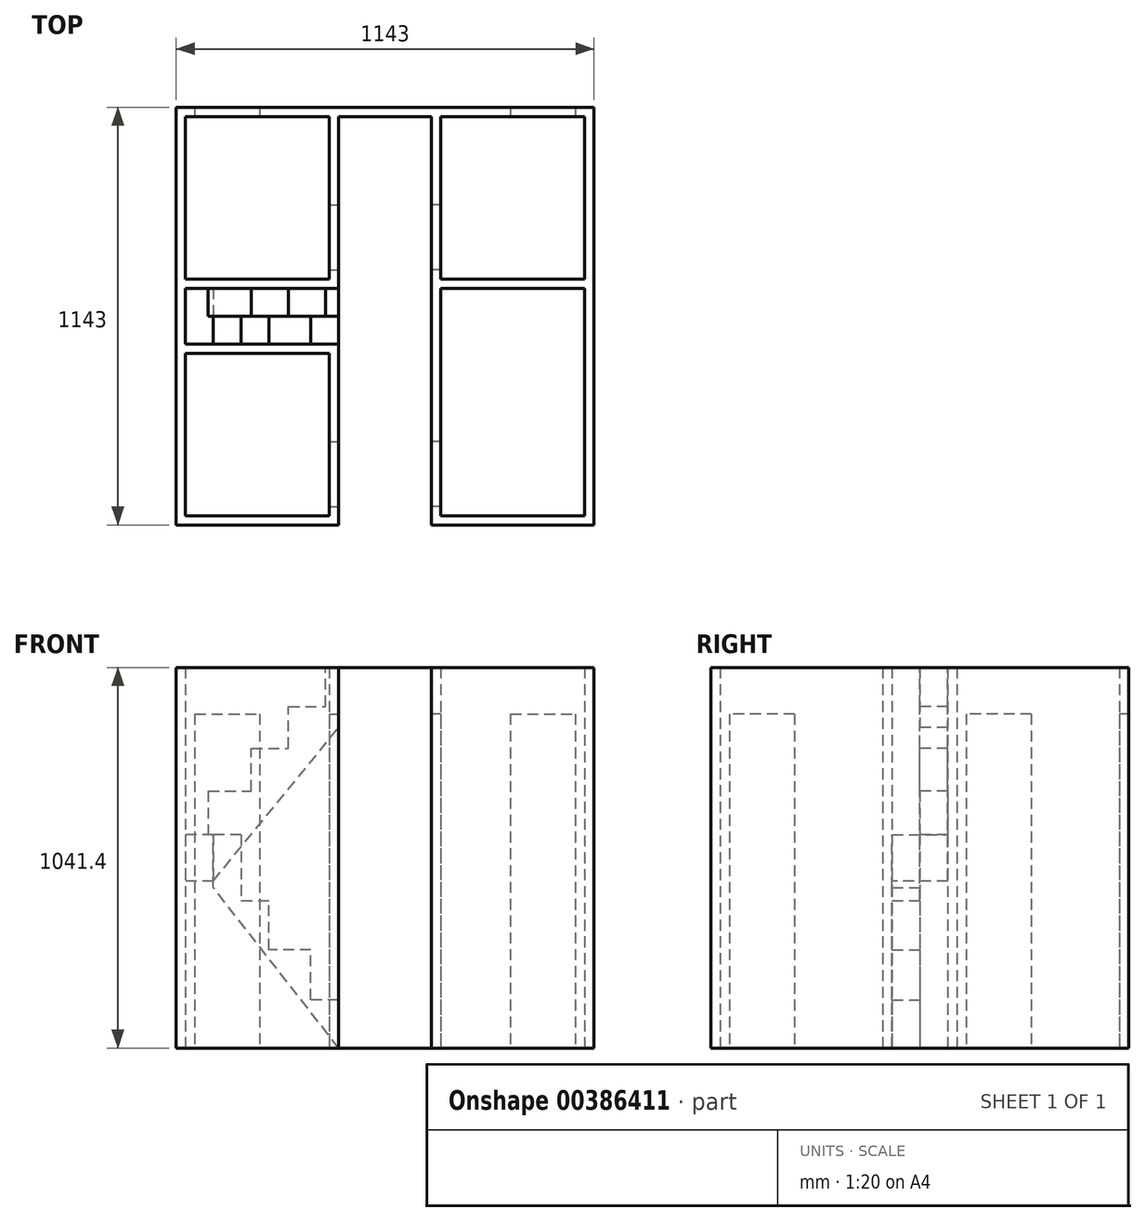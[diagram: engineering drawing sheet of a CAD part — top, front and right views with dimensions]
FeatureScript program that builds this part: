
annotation { "Feature Type Name" : "Feature", "Feature Type Description" : "" }
export const myFeature = defineFeature(function(context is Context, id is Id, definition is map)
    precondition{}
    {
        {
            var Q0;
            Q0=qCreatedBy(makeId("Top.planeOp"),FACE);
            var sketch = newSketch(context, id + "F0", { "sketchPlane" : qUnion([Q0])});
            skLineSegment(sketch, "E0.bottom", {"start": v(-571.5, 571.5) * mm, "end": v(-571.5, 571.5) * mm});
            skLineSegment(sketch, "E0.top", {"start": v(-571.5, -571.5) * mm, "end": v(-152.4, -571.5) * mm});
            skLineSegment(sketch, "E0.left", {"start": v(-571.5, 571.5) * mm, "end": v(-571.5, 76.2) * mm});
            skLineSegment(sketch, "E0.right", {"start": v(571.5, 571.5) * mm, "end": v(571.5, 76.2) * mm});
            skPoint(sketch, "E0.middle", {"position": v(0, 0) * mm});
            skLineSegment(sketch, "E1", {"start": v(0, 571.5) * mm, "end": v(0, -571.5) * mm, "construction": true});
            skLineSegment(sketch, "E2", {"start": v(-571.5, 0) * mm, "end": v(0, 0) * mm, "construction": true});
            skLineSegment(sketch, "E3", {"start": v(571.5, -571.5) * mm, "end": v(0, 0) * mm, "construction": true});
            skLineSegment(sketch, "E4", {"start": v(-571.5, -571.5) * mm, "end": v(571.5, 571.5) * mm, "construction": true});
            skPoint(sketch, "E5.orphan", {"position": v(571.5, 0) * mm});
            skLineSegment(sketch, "E6.0", {"start": v(-571.5, 76.2) * mm, "end": v(-127, 76.2) * mm});
            skLineSegment(sketch, "E7.0", {"start": v(-571.5, -76.2) * mm, "end": v(-152.4, -76.2) * mm});
            skLineSegment(sketch, "E8.0", {"start": v(-127, 571.5) * mm, "end": v(-127, 103.05) * mm});
            skLineSegment(sketch, "E9.0", {"start": v(127, 571.5) * mm, "end": v(127, 571.5) * mm});
            skLineSegment(sketch, "E10", {"start": v(127, 76.2) * mm, "end": v(127, 76.2) * mm});
            skLineSegment(sketch, "E11", {"start": v(127, 571.5) * mm, "end": v(127, 101.6) * mm});
            skLineSegment(sketch, "E12", {"start": v(-127, 571.5) * mm, "end": v(546.1, 571.5) * mm});
            skLineSegment(sketch, "E13", {"start": v(571.5, 571.5) * mm, "end": v(571.5, 571.5) * mm});
            skLineSegment(sketch, "E14", {"start": v(-571.5, 571.5) * mm, "end": v(-546.1, 571.5) * mm});
            skLineSegment(sketch, "E15", {"start": v(-571.5, 76.2) * mm, "end": v(-571.5, -76.2) * mm});
            skLineSegment(sketch, "E16", {"start": v(-571.5, -76.2) * mm, "end": v(-571.5, -571.5) * mm});
            skLineSegment(sketch, "E17", {"start": v(-127, -571.5) * mm, "end": v(127, -571.5) * mm});
            skLineSegment(sketch, "E18", {"start": v(127, -571.5) * mm, "end": v(571.5, -571.5) * mm});
            skLineSegment(sketch, "E19", {"start": v(127, 76.2) * mm, "end": v(571.5, 76.2) * mm});
            skLineSegment(sketch, "E20", {"start": v(571.5, 76.2) * mm, "end": v(571.5, -571.5) * mm});
            skLineSegment(sketch, "E21", {"start": v(-127, -76.2) * mm, "end": v(-127, -571.5) * mm});
            skLineSegment(sketch, "E22", {"start": v(0, 0) * mm, "end": v(-571.5, 571.5) * mm, "construction": true});
            skLineSegment(sketch, "E23.0", {"start": v(-127, 546.1) * mm, "end": v(571.5, 546.1) * mm});
            skLineSegment(sketch, "E23.1", {"start": v(-571.5, 546.1) * mm, "end": v(-546.1, 546.1) * mm});
            skLineSegment(sketch, "E24.0", {"start": v(546.1, 76.2) * mm, "end": v(546.1, -571.5) * mm});
            skLineSegment(sketch, "E24.1", {"start": v(546.1, 571.5) * mm, "end": v(546.1, 546.1) * mm});
            skLineSegment(sketch, "E25.0", {"start": v(127, 88.9) * mm, "end": v(571.5, 88.9) * mm});
            skLineSegment(sketch, "E26.0", {"start": v(127, -546.1) * mm, "end": v(571.5, -546.1) * mm});
            skLineSegment(sketch, "E26.1", {"start": v(-127, -546.1) * mm, "end": v(127, -546.1) * mm});
            skLineSegment(sketch, "E26.2", {"start": v(-571.5, -546.1) * mm, "end": v(-127, -546.1) * mm});
            skLineSegment(sketch, "E27.0", {"start": v(-546.1, -76.2) * mm, "end": v(-546.1, -571.5) * mm});
            skLineSegment(sketch, "E27.1", {"start": v(-546.1, 76.2) * mm, "end": v(-546.1, -76.2) * mm});
            skLineSegment(sketch, "E27.2", {"start": v(-546.1, 571.5) * mm, "end": v(-546.1, 76.2) * mm});
            skLineSegment(sketch, "E28.0", {"start": v(-571.5, 88.9) * mm, "end": v(-152.4, 88.9) * mm});
            skLineSegment(sketch, "E29.0", {"start": v(-571.5, -101.6) * mm, "end": v(-127, -101.6) * mm});
            skLineSegment(sketch, "E30.0", {"start": v(152.4, 571.5) * mm, "end": v(152.4, 101.59) * mm});
            skLineSegment(sketch, "E31.0", {"start": v(-152.4, -76.2) * mm, "end": v(-152.4, -101.6) * mm});
            skLineSegment(sketch, "E32.0", {"start": v(127, 101.6) * mm, "end": v(571.5, 101.6) * mm});
            skLineSegment(sketch, "E33.0", {"start": v(-571.5, 101.6) * mm, "end": v(-152.4, 101.6) * mm});
            skLineSegment(sketch, "E34", {"start": v(546.1, 546.1) * mm, "end": v(546.1, 76.2) * mm});
            skLineSegment(sketch, "E35", {"start": v(546.1, 571.5) * mm, "end": v(571.5, 571.5) * mm});
            skLineSegment(sketch, "E36", {"start": v(-546.1, 546.1) * mm, "end": v(-127, 546.1) * mm});
            skLineSegment(sketch, "E37", {"start": v(-546.1, 571.5) * mm, "end": v(-127, 571.5) * mm});
            skLineSegment(sketch, "E38", {"start": v(127, 101.6) * mm, "end": v(127, -571.5) * mm});
            skLineSegment(sketch, "E39", {"start": v(152.4, 101.59) * mm, "end": v(152.4, -571.5) * mm});
            skLineSegment(sketch, "E40", {"start": v(-152.4, -571.5) * mm, "end": v(-127, -571.5) * mm});
            skLineSegment(sketch, "E41", {"start": v(-152.4, -546.1) * mm, "end": v(-152.4, -571.5) * mm});
            skLineSegment(sketch, "E42", {"start": v(-127, -571.5) * mm, "end": v(-127, -571.5) * mm});
            skLineSegment(sketch, "E43", {"start": v(-152.4, -101.6) * mm, "end": v(-152.4, -546.1) * mm});
            skLineSegment(sketch, "E44", {"start": v(-152.4, -76.2) * mm, "end": v(-127, -76.2) * mm});
            skLineSegment(sketch, "E45.1", {"start": v(-152.4, 571.5) * mm, "end": v(-152.4, 101.6) * mm});
            skPoint(sketch, "E46.trimOffspring.end.orphan", {"position": v(0, 76.2) * mm});
            skLineSegment(sketch, "E47.0", {"start": v(342.9, 571.5) * mm, "end": v(342.9, 546.1) * mm});
            skLineSegment(sketch, "E48.0", {"start": v(520.7, 571.5) * mm, "end": v(520.7, 546.1) * mm});
            skLineSegment(sketch, "E49.0", {"start": v(-520.7, 571.5) * mm, "end": v(-520.7, 546.1) * mm});
            skLineSegment(sketch, "E50.0", {"start": v(-342.9, 571.5) * mm, "end": v(-342.9, 546.1) * mm});
            skLineSegment(sketch, "E51.0", {"start": v(-152.4, -520.7) * mm, "end": v(-127, -520.7) * mm});
            skLineSegment(sketch, "E52.0", {"start": v(-152.4, -342.9) * mm, "end": v(-127, -342.9) * mm});
            skLineSegment(sketch, "E53.MirrorCS", {"start": v(152.4, -520.7) * mm, "end": v(127, -520.7) * mm});
            skLineSegment(sketch, "E54.MirrorCS", {"start": v(152.4, -342.9) * mm, "end": v(127, -342.9) * mm});
            skLineSegment(sketch, "E55", {"start": v(-152.4, 101.6) * mm, "end": v(-152.4, 76.2) * mm});
            skLineSegment(sketch, "E56", {"start": v(-127, 103.05) * mm, "end": v(-127, 101.6) * mm});
            skLineSegment(sketch, "E57", {"start": v(-152.4, 101.6) * mm, "end": v(-152.4, 101.6) * mm});
            skLineSegment(sketch, "E58", {"start": v(-127, 101.6) * mm, "end": v(-127, 76.2) * mm});
            skLineSegment(sketch, "E59", {"start": v(-152.4, 101.6) * mm, "end": v(-127, 101.6) * mm});
            skLineSegment(sketch, "E60.0", {"start": v(-152.4, 127) * mm, "end": v(-127, 127) * mm});
            skLineSegment(sketch, "E61.0", {"start": v(-152.4, 304.8) * mm, "end": v(-127, 304.8) * mm});
            skLineSegment(sketch, "E62.MirrorCS", {"start": v(152.4, 127) * mm, "end": v(127, 127) * mm});
            skLineSegment(sketch, "E63.MirrorCS", {"start": v(152.4, 304.8) * mm, "end": v(127, 304.8) * mm});
            skSolve(sketch);
        }
        {
            var Q0;
            {var subQ0=sQuery(id+"F0.wireOp",EDGE,"E31.0");Q0=makeQuery(id+"F0.imprint","IMPRINT",FACE,{"disambiguationData":[TD([[makeQuery(id+"F0.imprint","IMPRINT",EDGE,{"derivedFrom":subQ0}),-1.0]])]});}
            var Q1;
            {var subQ4=sQuery(id+"F0.wireOp",EDGE,"E31.0");Q1=makeQuery(id+"F0.imprint","IMPRINT",FACE,{"disambiguationData":[TD([[makeQuery(id+"F0.imprint","IMPRINT",EDGE,{"derivedFrom":subQ4}),1.0]])]});}
            var Q2;
            {var subQ3=sQuery(id+"F0.wireOp",EDGE,"E52.0");Q2=makeQuery(id+"F0.imprint","IMPRINT",FACE,{"disambiguationData":[TD([[makeQuery(id+"F0.imprint","IMPRINT",EDGE,{"derivedFrom":subQ3}),1.0]])]});}
            var Q3;
            {var subQ0=sQuery(id+"F0.wireOp",EDGE,"E26.2");var subQ1=sQuery(id+"F0.wireOp",EDGE,"E16");var subQ2=makeQuery(id+"F0.imprint","INTERSECT",VERTEX,{"derivedFrom":[subQ1,subQ0]});Q3=makeQuery(id+"F0.imprint","IMPRINT",FACE,{"disambiguationData":[TD([[makeQuery(id+"F0.imprint","IMPRINT",EDGE,{"disambiguationData":[TD([[subQ2,1.0]])],"derivedFrom":subQ1}),1.0]])]});}
            var Q4;
            {var subQ0=sQuery(id+"F0.wireOp",EDGE,"E16");var subQ5=sQuery(id+"F0.wireOp",EDGE,"E29.0");var subQ6=makeQuery(id+"F0.imprint","INTERSECT",VERTEX,{"derivedFrom":[subQ0,subQ5]});Q4=makeQuery(id+"F0.imprint","IMPRINT",FACE,{"disambiguationData":[TD([[makeQuery(id+"F0.imprint","IMPRINT",EDGE,{"disambiguationData":[TD([[subQ6,-1.0]])],"derivedFrom":subQ5}),1.0]])]});}
            var Q5;
            {var subQ0=sQuery(id+"F0.wireOp",EDGE,"E15");Q5=makeQuery(id+"F0.imprint","IMPRINT",FACE,{"disambiguationData":[TD([[makeQuery(id+"F0.imprint","IMPRINT",EDGE,{"derivedFrom":subQ0}),1.0]])]});}
            var Q6;
            {var subQ1=sQuery(id+"F0.wireOp",EDGE,"E0.left");var subQ3=sQuery(id+"F0.wireOp",EDGE,"E28.0");var subQ4=makeQuery(id+"F0.imprint","INTERSECT",VERTEX,{"derivedFrom":[subQ1,subQ3]});Q6=makeQuery(id+"F0.imprint","IMPRINT",FACE,{"disambiguationData":[TD([[makeQuery(id+"F0.imprint","IMPRINT",EDGE,{"disambiguationData":[TD([[subQ4,-1.0]])],"derivedFrom":subQ3}),-1.0]])]});}
            var Q7;
            {var subQ0=sQuery(id+"F0.wireOp",EDGE,"E28.0");var subQ1=sQuery(id+"F0.wireOp",EDGE,"E0.left");var subQ2=makeQuery(id+"F0.imprint","INTERSECT",VERTEX,{"derivedFrom":[subQ1,subQ0]});Q7=makeQuery(id+"F0.imprint","IMPRINT",FACE,{"disambiguationData":[TD([[makeQuery(id+"F0.imprint","IMPRINT",EDGE,{"disambiguationData":[TD([[subQ2,1.0]])],"derivedFrom":subQ1}),1.0]])]});}
            var Q8;
            {var subQ0=sQuery(id+"F0.wireOp",EDGE,"E23.1");Q8=makeQuery(id+"F0.imprint","IMPRINT",FACE,{"disambiguationData":[TD([[makeQuery(id+"F0.imprint","IMPRINT",EDGE,{"derivedFrom":subQ0}),-1.0]])]});}
            var Q9;
            {var subQ0=sQuery(id+"F0.wireOp",EDGE,"E14");Q9=makeQuery(id+"F0.imprint","IMPRINT",FACE,{"disambiguationData":[TD([[makeQuery(id+"F0.imprint","IMPRINT",EDGE,{"derivedFrom":subQ0}),-1.0]])]});}
            var Q10;
            {var subQ5=sQuery(id+"F0.wireOp",EDGE,"E49.0");Q10=makeQuery(id+"F0.imprint","IMPRINT",FACE,{"disambiguationData":[TD([[makeQuery(id+"F0.imprint","IMPRINT",EDGE,{"derivedFrom":subQ5}),-1.0]])]});}
            var Q11;
            {var subQ0=sQuery(id+"F0.wireOp",EDGE,"E50.0");Q11=makeQuery(id+"F0.imprint","IMPRINT",FACE,{"disambiguationData":[TD([[makeQuery(id+"F0.imprint","IMPRINT",EDGE,{"derivedFrom":subQ0}),1.0]])]});}
            var Q12;
            {var subQ0=sQuery(id+"F0.wireOp",EDGE,"E37");var subQ5=sQuery(id+"F0.wireOp",EDGE,"E45.1");var subQ7=makeQuery(id+"F0.imprint","INTERSECT",VERTEX,{"derivedFrom":[subQ0,subQ5]});Q12=makeQuery(id+"F0.imprint","IMPRINT",FACE,{"disambiguationData":[TD([[makeQuery(id+"F0.imprint","IMPRINT",EDGE,{"disambiguationData":[TD([[subQ7,-1.0]])],"derivedFrom":subQ5}),1.0]])]});}
            var Q13;
            {var subQ3=sQuery(id+"F0.wireOp",EDGE,"E61.0");Q13=makeQuery(id+"F0.imprint","IMPRINT",FACE,{"disambiguationData":[TD([[makeQuery(id+"F0.imprint","IMPRINT",EDGE,{"derivedFrom":subQ3}),1.0]])]});}
            var Q14;
            {var subQ1=sQuery(id+"F0.wireOp",EDGE,"E56");Q14=makeQuery(id+"F0.imprint","IMPRINT",FACE,{"disambiguationData":[TD([[makeQuery(id+"F0.imprint","IMPRINT",EDGE,{"derivedFrom":subQ1}),-1.0]])]});}
            var Q15;
            {var subQ0=sQuery(id+"F0.wireOp",EDGE,"E58");Q15=makeQuery(id+"F0.imprint","IMPRINT",FACE,{"disambiguationData":[TD([[makeQuery(id+"F0.imprint","IMPRINT",EDGE,{"derivedFrom":subQ0}),-1.0]])]});}
            var Q16;
            {var subQ0=sQuery(id+"F0.wireOp",EDGE,"E33.0");var subQ1=sQuery(id+"F0.wireOp",EDGE,"E27.2");var subQ2=makeQuery(id+"F0.imprint","INTERSECT",VERTEX,{"derivedFrom":[subQ1,subQ0]});Q16=makeQuery(id+"F0.imprint","IMPRINT",FACE,{"disambiguationData":[TD([[makeQuery(id+"F0.imprint","IMPRINT",EDGE,{"disambiguationData":[TD([[subQ2,-1.0]])],"derivedFrom":subQ1}),1.0]])]});}
            var Q17;
            {var subQ3=sQuery(id+"F0.wireOp",EDGE,"E55");var subQ5=sQuery(id+"F0.wireOp",EDGE,"E28.0");var subQ6=makeQuery(id+"F0.imprint","INTERSECT",VERTEX,{"derivedFrom":[subQ5,subQ3]});Q17=makeQuery(id+"F0.imprint","IMPRINT",FACE,{"disambiguationData":[TD([[makeQuery(id+"F0.imprint","IMPRINT",EDGE,{"disambiguationData":[TD([[subQ6,1.0]])],"derivedFrom":subQ5}),-1.0]])]});}
            var Q18;
            {var subQ3=sQuery(id+"F0.wireOp",EDGE,"E39");var subQ5=sQuery(id+"F0.wireOp",EDGE,"E25.0");var subQ6=makeQuery(id+"F0.imprint","INTERSECT",VERTEX,{"derivedFrom":[subQ5,subQ3]});Q18=makeQuery(id+"F0.imprint","IMPRINT",FACE,{"disambiguationData":[TD([[makeQuery(id+"F0.imprint","IMPRINT",EDGE,{"disambiguationData":[TD([[subQ6,-1.0]])],"derivedFrom":subQ5}),-1.0]])]});}
            var Q19;
            {var subQ1=sQuery(id+"F0.wireOp",EDGE,"E25.0");var subQ7=sQuery(id+"F0.wireOp",EDGE,"E39");var subQ9=makeQuery(id+"F0.imprint","INTERSECT",VERTEX,{"derivedFrom":[subQ1,subQ7]});Q19=makeQuery(id+"F0.imprint","IMPRINT",FACE,{"disambiguationData":[TD([[makeQuery(id+"F0.imprint","IMPRINT",EDGE,{"disambiguationData":[TD([[subQ9,-1.0]])],"derivedFrom":subQ1}),1.0]])]});}
            var Q20;
            {var subQ0=sQuery(id+"F0.wireOp",EDGE,"E38");var subQ3=sQuery(id+"F0.wireOp",EDGE,"E25.0");var subQ4=makeQuery(id+"F0.imprint","INTERSECT",VERTEX,{"derivedFrom":[subQ3,subQ0]});Q20=makeQuery(id+"F0.imprint","IMPRINT",FACE,{"disambiguationData":[TD([[makeQuery(id+"F0.imprint","IMPRINT",EDGE,{"disambiguationData":[TD([[subQ4,-1.0]])],"derivedFrom":subQ3}),1.0]])]});}
            var Q21;
            {var subQ3=sQuery(id+"F0.wireOp",EDGE,"E62.MirrorCS");Q21=makeQuery(id+"F0.imprint","IMPRINT",FACE,{"disambiguationData":[TD([[makeQuery(id+"F0.imprint","IMPRINT",EDGE,{"derivedFrom":subQ3}),1.0]])]});}
            var Q22;
            {var subQ0=sQuery(id+"F0.wireOp",EDGE,"E38");var subQ1=sQuery(id+"F0.wireOp",EDGE,"E19");var subQ2=makeQuery(id+"F0.imprint","INTERSECT",VERTEX,{"derivedFrom":[subQ1,subQ0]});Q22=makeQuery(id+"F0.imprint","IMPRINT",FACE,{"disambiguationData":[TD([[makeQuery(id+"F0.imprint","IMPRINT",EDGE,{"disambiguationData":[TD([[subQ2,-1.0]])],"derivedFrom":subQ1}),1.0]])]});}
            var Q23;
            {var subQ5=sQuery(id+"F0.wireOp",EDGE,"E54.MirrorCS");Q23=makeQuery(id+"F0.imprint","IMPRINT",FACE,{"disambiguationData":[TD([[makeQuery(id+"F0.imprint","IMPRINT",EDGE,{"derivedFrom":subQ5}),-1.0]])]});}
            var Q24;
            {var subQ5=sQuery(id+"F0.wireOp",EDGE,"E53.MirrorCS");Q24=makeQuery(id+"F0.imprint","IMPRINT",FACE,{"disambiguationData":[TD([[makeQuery(id+"F0.imprint","IMPRINT",EDGE,{"derivedFrom":subQ5}),1.0]])]});}
            var Q25;
            {var subQ3=sQuery(id+"F0.wireOp",EDGE,"E51.0");Q25=makeQuery(id+"F0.imprint","IMPRINT",FACE,{"disambiguationData":[TD([[makeQuery(id+"F0.imprint","IMPRINT",EDGE,{"derivedFrom":subQ3}),-1.0]])]});}
            var Q26;
            {var subQ0=sQuery(id+"F0.wireOp",EDGE,"E41");Q26=makeQuery(id+"F0.imprint","IMPRINT",FACE,{"disambiguationData":[TD([[makeQuery(id+"F0.imprint","IMPRINT",EDGE,{"derivedFrom":subQ0}),-1.0]])]});}
            var Q27;
            {var subQ0=sQuery(id+"F0.wireOp",EDGE,"E16");var subQ1=sQuery(id+"F0.wireOp",EDGE,"E0.top");var subQ2=makeQuery(id+"F0.imprint","INTERSECT",VERTEX,{"derivedFrom":[subQ1,subQ0]});Q27=makeQuery(id+"F0.imprint","IMPRINT",FACE,{"disambiguationData":[TD([[makeQuery(id+"F0.imprint","IMPRINT",EDGE,{"disambiguationData":[TD([[subQ2,-1.0]])],"derivedFrom":subQ1}),1.0]])]});}
            var Q28;
            {var subQ0=sQuery(id+"F0.wireOp",EDGE,"E40");Q28=makeQuery(id+"F0.imprint","IMPRINT",FACE,{"disambiguationData":[TD([[makeQuery(id+"F0.imprint","IMPRINT",EDGE,{"derivedFrom":subQ0}),1.0]])]});}
            var Q29;
            {var subQ1=sQuery(id+"F0.wireOp",EDGE,"E18");var subQ3=sQuery(id+"F0.wireOp",EDGE,"E39");var subQ4=makeQuery(id+"F0.imprint","INTERSECT",VERTEX,{"derivedFrom":[subQ1,subQ3]});Q29=makeQuery(id+"F0.imprint","IMPRINT",FACE,{"disambiguationData":[TD([[makeQuery(id+"F0.imprint","IMPRINT",EDGE,{"disambiguationData":[TD([[subQ4,1.0]])],"derivedFrom":subQ3}),-1.0]])]});}
            var Q30;
            {var subQ0=sQuery(id+"F0.wireOp",EDGE,"E24.0");var subQ1=sQuery(id+"F0.wireOp",EDGE,"E18");var subQ2=makeQuery(id+"F0.imprint","INTERSECT",VERTEX,{"derivedFrom":[subQ1,subQ0]});Q30=makeQuery(id+"F0.imprint","IMPRINT",FACE,{"disambiguationData":[TD([[makeQuery(id+"F0.imprint","IMPRINT",EDGE,{"disambiguationData":[TD([[subQ2,1.0]])],"derivedFrom":subQ1}),1.0]])]});}
            var Q31;
            {var subQ0=sQuery(id+"F0.wireOp",EDGE,"E20");var subQ5=sQuery(id+"F0.wireOp",EDGE,"E26.0");var subQ7=makeQuery(id+"F0.imprint","INTERSECT",VERTEX,{"derivedFrom":[subQ0,subQ5]});Q31=makeQuery(id+"F0.imprint","IMPRINT",FACE,{"disambiguationData":[TD([[makeQuery(id+"F0.imprint","IMPRINT",EDGE,{"disambiguationData":[TD([[subQ7,1.0]])],"derivedFrom":subQ5}),1.0]])]});}
            var Q32;
            {var subQ0=sQuery(id+"F0.wireOp",EDGE,"E20");var subQ1=sQuery(id+"F0.wireOp",EDGE,"E18");var subQ2=makeQuery(id+"F0.imprint","INTERSECT",VERTEX,{"derivedFrom":[subQ1,subQ0]});Q32=makeQuery(id+"F0.imprint","IMPRINT",FACE,{"disambiguationData":[TD([[makeQuery(id+"F0.imprint","IMPRINT",EDGE,{"disambiguationData":[TD([[subQ2,1.0]])],"derivedFrom":subQ1}),1.0]])]});}
            var Q33;
            {var subQ0=sQuery(id+"F0.wireOp",EDGE,"E25.0");var subQ1=sQuery(id+"F0.wireOp",EDGE,"E0.right");var subQ2=makeQuery(id+"F0.imprint","INTERSECT",VERTEX,{"derivedFrom":[subQ1,subQ0]});Q33=makeQuery(id+"F0.imprint","IMPRINT",FACE,{"disambiguationData":[TD([[makeQuery(id+"F0.imprint","IMPRINT",EDGE,{"disambiguationData":[TD([[subQ2,1.0]])],"derivedFrom":subQ1}),-1.0]])]});}
            var Q34;
            {var subQ1=sQuery(id+"F0.wireOp",EDGE,"E0.right");var subQ3=sQuery(id+"F0.wireOp",EDGE,"E25.0");var subQ4=makeQuery(id+"F0.imprint","INTERSECT",VERTEX,{"derivedFrom":[subQ1,subQ3]});Q34=makeQuery(id+"F0.imprint","IMPRINT",FACE,{"disambiguationData":[TD([[makeQuery(id+"F0.imprint","IMPRINT",EDGE,{"disambiguationData":[TD([[subQ4,1.0]])],"derivedFrom":subQ3}),-1.0]])]});}
            var Q35;
            {var subQ0=sQuery(id+"F0.wireOp",EDGE,"E23.0");var subQ1=sQuery(id+"F0.wireOp",EDGE,"E0.right");var subQ2=makeQuery(id+"F0.imprint","INTERSECT",VERTEX,{"derivedFrom":[subQ1,subQ0]});Q35=makeQuery(id+"F0.imprint","IMPRINT",FACE,{"disambiguationData":[TD([[makeQuery(id+"F0.imprint","IMPRINT",EDGE,{"disambiguationData":[TD([[subQ2,-1.0]])],"derivedFrom":subQ1}),-1.0]])]});}
            var Q36;
            {var subQ4=sQuery(id+"F0.wireOp",EDGE,"E24.1");Q36=makeQuery(id+"F0.imprint","IMPRINT",FACE,{"disambiguationData":[TD([[makeQuery(id+"F0.imprint","IMPRINT",EDGE,{"derivedFrom":subQ4}),1.0]])]});}
            var Q37;
            {var subQ0=sQuery(id+"F0.wireOp",EDGE,"E24.1");Q37=makeQuery(id+"F0.imprint","IMPRINT",FACE,{"disambiguationData":[TD([[makeQuery(id+"F0.imprint","IMPRINT",EDGE,{"derivedFrom":subQ0}),-1.0]])]});}
            var Q38;
            {var subQ3=sQuery(id+"F0.wireOp",EDGE,"E47.0");Q38=makeQuery(id+"F0.imprint","IMPRINT",FACE,{"disambiguationData":[TD([[makeQuery(id+"F0.imprint","IMPRINT",EDGE,{"derivedFrom":subQ3}),-1.0]])]});}
            var Q39;
            {var subQ0=sQuery(id+"F0.wireOp",EDGE,"E12");var subQ1=sQuery(id+"F0.wireOp",EDGE,"E11");var subQ2=makeQuery(id+"F0.imprint","INTERSECT",VERTEX,{"derivedFrom":[subQ1,subQ0]});Q39=makeQuery(id+"F0.imprint","IMPRINT",FACE,{"disambiguationData":[TD([[makeQuery(id+"F0.imprint","IMPRINT",EDGE,{"disambiguationData":[TD([[subQ2,-1.0]])],"derivedFrom":subQ1}),1.0]])]});}
            var Q40;
            {var subQ0=sQuery(id+"F0.wireOp",EDGE,"E63.MirrorCS");Q40=makeQuery(id+"F0.imprint","IMPRINT",FACE,{"disambiguationData":[TD([[makeQuery(id+"F0.imprint","IMPRINT",EDGE,{"derivedFrom":subQ0}),-1.0]])]});}
            var Q41;
            {var subQ0=sQuery(id+"F0.wireOp",EDGE,"E12");var subQ5=sQuery(id+"F0.wireOp",EDGE,"E11");var subQ6=makeQuery(id+"F0.imprint","INTERSECT",VERTEX,{"derivedFrom":[subQ5,subQ0]});Q41=makeQuery(id+"F0.imprint","IMPRINT",FACE,{"disambiguationData":[TD([[makeQuery(id+"F0.imprint","IMPRINT",EDGE,{"disambiguationData":[TD([[subQ6,-1.0]])],"derivedFrom":subQ5}),-1.0]])]});}
            extrude(context, id + "F1", {"entities" : qUnion([Q0, Q1, Q2, Q3, Q4, Q5, Q6, Q7, Q8, Q9, Q10, Q11, Q12, Q13, Q14, Q15, Q16, Q17, Q18, Q19, Q20, Q21, Q22, Q23, Q24, Q25, Q26, Q27, Q28, Q29, Q30, Q31, Q32, Q33, Q34, Q35, Q36, Q37, Q38, Q39, Q40, Q41]), "depth" : 1016 * mm, "hasSecondDirection" : true, "secondDirectionOppositeDirection" : true, "secondDirectionDepth" : 25.4 * mm});
        }
        {
            var Q0;
            Q0=makeQuery(id+"F1.opExtrude","CAP_FACE",FACE,{"disambiguationData":[OSD([sQuery(id+"F0.wireOp",EDGE,"E0.right"),sQuery(id+"F0.wireOp",EDGE,"E11"),sQuery(id+"F0.wireOp",EDGE,"E12"),sQuery(id+"F0.wireOp",EDGE,"E18"),sQuery(id+"F0.wireOp",EDGE,"E19"),sQuery(id+"F0.wireOp",EDGE,"E20"),sQuery(id+"F0.wireOp",EDGE,"E23.0"),sQuery(id+"F0.wireOp",EDGE,"E24.0"),sQuery(id+"F0.wireOp",EDGE,"E26.0"),sQuery(id+"F0.wireOp",EDGE,"E30.0"),sQuery(id+"F0.wireOp",EDGE,"E32.0"),sQuery(id+"F0.wireOp",EDGE,"E34"),sQuery(id+"F0.wireOp",EDGE,"E35"),sQuery(id+"F0.wireOp",EDGE,"E38"),sQuery(id+"F0.wireOp",EDGE,"E39"),sQuery(id+"F0.wireOp",EDGE,"E48.0"),sQuery(id+"F0.wireOp",EDGE,"E53.MirrorCS"),sQuery(id+"F0.wireOp",EDGE,"E54.MirrorCS"),sQuery(id+"F0.wireOp",EDGE,"E62.MirrorCS")])],"isStart":false});
            var sketch = newSketch(context, id + "F2", { "sketchPlane" : qUnion([Q0])});
            skLineSegment(sketch, "E64.0", {"start": v(-546.1, 571.5) * mm, "end": v(-127, 571.5) * mm});
            skLineSegment(sketch, "E64.1", {"start": v(-546.1, 546.1) * mm, "end": v(-127, 546.1) * mm});
            skLineSegment(sketch, "E64.2", {"start": v(-520.7, 571.5) * mm, "end": v(-520.7, 546.1) * mm});
            skLineSegment(sketch, "E64.3", {"start": v(-342.9, 571.5) * mm, "end": v(-342.9, 546.1) * mm});
            skLineSegment(sketch, "E65.0", {"start": v(-152.4, 571.5) * mm, "end": v(-152.4, 101.6) * mm});
            skLineSegment(sketch, "E65.1", {"start": v(-127, 571.5) * mm, "end": v(-127, 103.05) * mm});
            skLineSegment(sketch, "E65.2", {"start": v(-152.4, 304.8) * mm, "end": v(-127, 304.8) * mm});
            skLineSegment(sketch, "E65.3", {"start": v(-152.4, 127) * mm, "end": v(-127, 127) * mm});
            skLineSegment(sketch, "E66.0", {"start": v(127, 571.5) * mm, "end": v(127, 101.6) * mm});
            skLineSegment(sketch, "E66.1", {"start": v(152.4, 304.8) * mm, "end": v(127, 304.8) * mm});
            skLineSegment(sketch, "E66.2", {"start": v(152.4, 571.5) * mm, "end": v(152.4, 101.59) * mm});
            skLineSegment(sketch, "E66.3", {"start": v(152.4, 127) * mm, "end": v(127, 127) * mm});
            skLineSegment(sketch, "E66.4", {"start": v(-127, 546.1) * mm, "end": v(571.5, 546.1) * mm});
            skLineSegment(sketch, "E66.5", {"start": v(-127, 571.5) * mm, "end": v(546.1, 571.5) * mm});
            skLineSegment(sketch, "E66.6", {"start": v(342.9, 571.5) * mm, "end": v(342.9, 546.1) * mm});
            skLineSegment(sketch, "E66.7", {"start": v(520.7, 571.5) * mm, "end": v(520.7, 546.1) * mm});
            skLineSegment(sketch, "E67.0", {"start": v(-127, -76.2) * mm, "end": v(-127, -571.5) * mm});
            skLineSegment(sketch, "E67.1", {"start": v(-152.4, -342.9) * mm, "end": v(-127, -342.9) * mm});
            skLineSegment(sketch, "E67.2", {"start": v(-152.4, -101.6) * mm, "end": v(-152.4, -546.1) * mm});
            skLineSegment(sketch, "E67.3", {"start": v(-152.4, -520.7) * mm, "end": v(-127, -520.7) * mm});
            skLineSegment(sketch, "E67.4", {"start": v(152.4, -520.7) * mm, "end": v(127, -520.7) * mm});
            skLineSegment(sketch, "E67.5", {"start": v(152.4, 101.59) * mm, "end": v(152.4, -571.5) * mm});
            skLineSegment(sketch, "E67.6", {"start": v(127, 101.6) * mm, "end": v(127, -571.5) * mm});
            skLineSegment(sketch, "E67.7", {"start": v(152.4, -342.9) * mm, "end": v(127, -342.9) * mm});
            skSolve(sketch);
        }
        {
            var Q0;
            {var subQ0=sQuery(id+"F2.wireOp",EDGE,"E64.2");Q0=makeQuery(id+"F2.imprint","IMPRINT",FACE,{"disambiguationData":[TD([[makeQuery(id+"F2.imprint","IMPRINT",EDGE,{"derivedFrom":subQ0}),1.0]])]});}
            var Q1;
            {var subQ0=sQuery(id+"F2.wireOp",EDGE,"E67.1");Q1=makeQuery(id+"F2.imprint","IMPRINT",FACE,{"disambiguationData":[TD([[makeQuery(id+"F2.imprint","IMPRINT",EDGE,{"derivedFrom":subQ0}),-1.0]])]});}
            var Q2;
            {var subQ0=sQuery(id+"F2.wireOp",EDGE,"E67.4");Q2=makeQuery(id+"F2.imprint","IMPRINT",FACE,{"disambiguationData":[TD([[makeQuery(id+"F2.imprint","IMPRINT",EDGE,{"derivedFrom":subQ0}),-1.0]])]});}
            var Q3;
            {var subQ2=sQuery(id+"F2.wireOp",EDGE,"E66.6");Q3=makeQuery(id+"F2.imprint","IMPRINT",FACE,{"disambiguationData":[TD([[makeQuery(id+"F2.imprint","IMPRINT",EDGE,{"derivedFrom":subQ2}),1.0]])]});}
            var Q4;
            {var subQ2=sQuery(id+"F2.wireOp",EDGE,"E66.1");Q4=makeQuery(id+"F2.imprint","IMPRINT",FACE,{"disambiguationData":[TD([[makeQuery(id+"F2.imprint","IMPRINT",EDGE,{"derivedFrom":subQ2}),1.0]])]});}
            var Q5;
            {var subQ0=sQuery(id+"F2.wireOp",EDGE,"E65.2");Q5=makeQuery(id+"F2.imprint","IMPRINT",FACE,{"disambiguationData":[TD([[makeQuery(id+"F2.imprint","IMPRINT",EDGE,{"derivedFrom":subQ0}),-1.0]])]});}
            extrude(context, id + "F3", {"entities" : qUnion([Q0, Q1, Q2, Q3, Q4, Q5]), "oppositeDirection" : true, "depth" : 127 * mm});
        }
        {
            var Q0;
            Q0=makeQuery(id+"F1.opExtrude","SWEPT_BODY",BODY,{"disambiguationData":[OSD([sQuery(id+"F0.wireOp",EDGE,"E0.top"),sQuery(id+"F0.wireOp",EDGE,"E0.left"),sQuery(id+"F0.wireOp",EDGE,"E6.0"),sQuery(id+"F0.wireOp",EDGE,"E7.0"),sQuery(id+"F0.wireOp",EDGE,"E8.0"),sQuery(id+"F0.wireOp",EDGE,"E14"),sQuery(id+"F0.wireOp",EDGE,"E15"),sQuery(id+"F0.wireOp",EDGE,"E16"),sQuery(id+"F0.wireOp",EDGE,"E21"),sQuery(id+"F0.wireOp",EDGE,"E26.2"),sQuery(id+"F0.wireOp",EDGE,"E27.0"),sQuery(id+"F0.wireOp",EDGE,"E27.1"),sQuery(id+"F0.wireOp",EDGE,"E27.2"),sQuery(id+"F0.wireOp",EDGE,"E29.0"),sQuery(id+"F0.wireOp",EDGE,"E33.0"),sQuery(id+"F0.wireOp",EDGE,"E36"),sQuery(id+"F0.wireOp",EDGE,"E37"),sQuery(id+"F0.wireOp",EDGE,"E40"),sQuery(id+"F0.wireOp",EDGE,"E43"),sQuery(id+"F0.wireOp",EDGE,"E44"),sQuery(id+"F0.wireOp",EDGE,"E45.1"),sQuery(id+"F0.wireOp",EDGE,"E49.0"),sQuery(id+"F0.wireOp",EDGE,"E51.0"),sQuery(id+"F0.wireOp",EDGE,"E52.0"),sQuery(id+"F0.wireOp",EDGE,"E56"),sQuery(id+"F0.wireOp",EDGE,"E58"),sQuery(id+"F0.wireOp",EDGE,"E60.0")])]});
            var Q1;
            Q1=makeQuery(id+"F1.opExtrude","SWEPT_BODY",BODY,{"disambiguationData":[OSD([sQuery(id+"F0.wireOp",EDGE,"E8.0"),sQuery(id+"F0.wireOp",EDGE,"E11"),sQuery(id+"F0.wireOp",EDGE,"E12"),sQuery(id+"F0.wireOp",EDGE,"E23.0"),sQuery(id+"F0.wireOp",EDGE,"E30.0"),sQuery(id+"F0.wireOp",EDGE,"E36"),sQuery(id+"F0.wireOp",EDGE,"E37"),sQuery(id+"F0.wireOp",EDGE,"E45.1"),sQuery(id+"F0.wireOp",EDGE,"E47.0"),sQuery(id+"F0.wireOp",EDGE,"E50.0"),sQuery(id+"F0.wireOp",EDGE,"E61.0"),sQuery(id+"F0.wireOp",EDGE,"E63.MirrorCS")])]});
            var Q2;
            Q2=makeQuery(id+"F3.opExtrude","SWEPT_BODY",BODY,{"disambiguationData":[OSD([sQuery(id+"F2.wireOp",EDGE,"E64.0"),sQuery(id+"F2.wireOp",EDGE,"E64.1"),sQuery(id+"F2.wireOp",EDGE,"E64.2"),sQuery(id+"F2.wireOp",EDGE,"E64.3")])]});
            var Q3;
            Q3=makeQuery(id+"F3.opExtrude","SWEPT_BODY",BODY,{"disambiguationData":[OSD([sQuery(id+"F2.wireOp",EDGE,"E65.0"),sQuery(id+"F2.wireOp",EDGE,"E65.1"),sQuery(id+"F2.wireOp",EDGE,"E65.2"),sQuery(id+"F2.wireOp",EDGE,"E65.3")])]});
            var Q4;
            Q4=makeQuery(id+"F3.opExtrude","SWEPT_BODY",BODY,{"disambiguationData":[OSD([sQuery(id+"F2.wireOp",EDGE,"E66.4"),sQuery(id+"F2.wireOp",EDGE,"E66.5"),sQuery(id+"F2.wireOp",EDGE,"E66.6"),sQuery(id+"F2.wireOp",EDGE,"E66.7")])]});
            var Q5;
            Q5=makeQuery(id+"F1.opExtrude","SWEPT_BODY",BODY,{"disambiguationData":[OSD([sQuery(id+"F0.wireOp",EDGE,"E0.right"),sQuery(id+"F0.wireOp",EDGE,"E11"),sQuery(id+"F0.wireOp",EDGE,"E12"),sQuery(id+"F0.wireOp",EDGE,"E18"),sQuery(id+"F0.wireOp",EDGE,"E19"),sQuery(id+"F0.wireOp",EDGE,"E20"),sQuery(id+"F0.wireOp",EDGE,"E23.0"),sQuery(id+"F0.wireOp",EDGE,"E24.0"),sQuery(id+"F0.wireOp",EDGE,"E26.0"),sQuery(id+"F0.wireOp",EDGE,"E30.0"),sQuery(id+"F0.wireOp",EDGE,"E32.0"),sQuery(id+"F0.wireOp",EDGE,"E34"),sQuery(id+"F0.wireOp",EDGE,"E35"),sQuery(id+"F0.wireOp",EDGE,"E38"),sQuery(id+"F0.wireOp",EDGE,"E39"),sQuery(id+"F0.wireOp",EDGE,"E48.0"),sQuery(id+"F0.wireOp",EDGE,"E53.MirrorCS"),sQuery(id+"F0.wireOp",EDGE,"E54.MirrorCS"),sQuery(id+"F0.wireOp",EDGE,"E62.MirrorCS")])]});
            var Q6;
            Q6=makeQuery(id+"F3.opExtrude","SWEPT_BODY",BODY,{"disambiguationData":[OSD([sQuery(id+"F2.wireOp",EDGE,"E66.0"),sQuery(id+"F2.wireOp",EDGE,"E66.1"),sQuery(id+"F2.wireOp",EDGE,"E66.2"),sQuery(id+"F2.wireOp",EDGE,"E66.3")])]});
            var Q7;
            Q7=makeQuery(id+"F3.opExtrude","SWEPT_BODY",BODY,{"disambiguationData":[OSD([sQuery(id+"F2.wireOp",EDGE,"E67.4"),sQuery(id+"F2.wireOp",EDGE,"E67.5"),sQuery(id+"F2.wireOp",EDGE,"E67.6"),sQuery(id+"F2.wireOp",EDGE,"E67.7")])]});
            var Q8;
            Q8=makeQuery(id+"F3.opExtrude","SWEPT_BODY",BODY,{"disambiguationData":[OSD([sQuery(id+"F2.wireOp",EDGE,"E67.0"),sQuery(id+"F2.wireOp",EDGE,"E67.1"),sQuery(id+"F2.wireOp",EDGE,"E67.2"),sQuery(id+"F2.wireOp",EDGE,"E67.3")])]});
            booleanBodies(context, id + "F4", {"operationType" : BooleanOperationType.UNION, "tools" : qUnion([Q0, Q1, Q2, Q3, Q4, Q5, Q6, Q7, Q8])});
        }
        {
            var Q0;
            Q0=makeQuery(id+"F1.opExtrude","SWEPT_FACE",FACE,{"disambiguationData":[OSD([sQuery(id+"F0.wireOp",EDGE,"E27.1")])]});
            var sketch = newSketch(context, id + "F5", { "sketchPlane" : qUnion([Q0])});
            skLineSegment(sketch, "E68.0", {"start": v(76.2, 1016) * mm, "end": v(76.2, -25.4) * mm});
            skLineSegment(sketch, "E68.1", {"start": v(76.2, -25.4) * mm, "end": v(-76.2, -25.4) * mm});
            skLineSegment(sketch, "E68.2", {"start": v(-76.2, 1016) * mm, "end": v(-76.2, -25.4) * mm});
            skLineSegment(sketch, "E68.3", {"start": v(76.2, 1016) * mm, "end": v(-76.2, 1016) * mm});
            skLineSegment(sketch, "E69", {"start": v(76.2, 431.8) * mm, "end": v(-76.2, 431.8) * mm});
            skLineSegment(sketch, "E70", {"start": v(-76.2, 558.8) * mm, "end": v(76.2, 558.8) * mm});
            skSolve(sketch);
        }
        {
            var Q0;
            {var subQ0=sQuery(id+"F5.wireOp",EDGE,"E69");Q0=makeQuery(id+"F5.imprint","IMPRINT",FACE,{"disambiguationData":[TD([[makeQuery(id+"F5.imprint","IMPRINT",EDGE,{"derivedFrom":subQ0}),-1.0]])]});}
            extrude(context, id + "F6", {"entities" : qUnion([Q0]), "depth" : 76.2 * mm});
        }
        {
            var Q0;
            Q0=makeQuery(id+"F6.opExtrude","CAP_FACE",FACE,{"disambiguationData":[OSD([sQuery(id+"F5.wireOp",EDGE,"E68.0"),sQuery(id+"F5.wireOp",EDGE,"E68.2"),sQuery(id+"F5.wireOp",EDGE,"E69"),sQuery(id+"F5.wireOp",EDGE,"E70")])],"isStart":false});
            var sketch = newSketch(context, id + "F7", { "sketchPlane" : qUnion([Q0])});
            skLineSegment(sketch, "E71.0", {"start": v(76.2, 431.8) * mm, "end": v(-76.2, 431.8) * mm});
            skLineSegment(sketch, "E71.1", {"start": v(-76.2, 558.8) * mm, "end": v(76.2, 558.8) * mm});
            skLineSegment(sketch, "E71.2", {"start": v(-76.2, 558.8) * mm, "end": v(-76.2, 431.8) * mm});
            skLineSegment(sketch, "E71.3", {"start": v(76.2, 558.8) * mm, "end": v(76.2, 431.8) * mm});
            skLineSegment(sketch, "E71.4", {"start": v(76.2, -25.4) * mm, "end": v(-76.2, -25.4) * mm});
            skLineSegment(sketch, "E71.5", {"start": v(-76.2, 1016) * mm, "end": v(-76.2, -25.4) * mm});
            skLineSegment(sketch, "E71.6", {"start": v(76.2, 1016) * mm, "end": v(76.2, -25.4) * mm});
            skLineSegment(sketch, "E71.7", {"start": v(76.2, 1016) * mm, "end": v(-76.2, 1016) * mm});
            skSolve(sketch);
        }
        {
            var Q0;
            Q0=sQuery(id+"F7.wireOp",EDGE,"E71.6");
            cPlane(context, id + "F8", {"entities" : qUnion([Q0]), "cplaneType" : CPlaneType.LINE_ANGLE, "offset" : 25.4 * mm, "angle" : 90 * degree, "oppositeDirection" : true, "width" : 152.4 * mm, "height" : 152.4 * mm});
        }
        {
            var Q0;
            Q0=qCreatedBy(id+"F8.planeOp",FACE);
            cPlane(context, id + "F9", {"entities" : qUnion([Q0]), "cplaneType" : CPlaneType.OFFSET, "offset" : 76.2 * mm, "width" : 152.4 * mm, "height" : 152.4 * mm});
        }
        {
            var Q0;
            Q0=qCreatedBy(id+"F9.planeOp",FACE);
            var sketch = newSketch(context, id + "F10", { "sketchPlane" : qUnion([Q0])});
            skLineSegment(sketch, "E72.2", {"start": v(-469.9, 558.8) * mm, "end": v(-546.1, 558.8) * mm});
            skLineSegment(sketch, "E72.3", {"start": v(-469.9, 1016) * mm, "end": v(-469.9, -25.4) * mm});
            skLineSegment(sketch, "E72.4", {"start": v(-469.9, 1016) * mm, "end": v(-469.9, -25.4) * mm});
            skLineSegment(sketch, "E72.5", {"start": v(-546.1, 1016) * mm, "end": v(-546.1, -25.4) * mm});
            skLineSegment(sketch, "E72.6", {"start": v(-546.1, 1016) * mm, "end": v(-546.1, -25.4) * mm});
            skLineSegment(sketch, "E72.7", {"start": v(-469.9, 558.8) * mm, "end": v(-546.1, 558.8) * mm});
            skLineSegment(sketch, "E73.0", {"start": v(-546.1, 1016) * mm, "end": v(-127, 1016) * mm});
            skLineSegment(sketch, "E73.1", {"start": v(-127, 1016) * mm, "end": v(-127, -25.4) * mm});
            skLineSegment(sketch, "E73.2", {"start": v(-546.1, -25.4) * mm, "end": v(-127, -25.4) * mm});
            skLineSegment(sketch, "E74.0", {"start": v(-469.9, 431.8) * mm, "end": v(-546.1, 431.8) * mm});
            skLineSegment(sketch, "E75", {"start": v(-469.9, 678.18) * mm, "end": v(-365.76, 678.18) * mm});
            skLineSegment(sketch, "E76", {"start": v(-365.76, 678.18) * mm, "end": v(-365.76, 795.02) * mm});
            skLineSegment(sketch, "E77", {"start": v(-365.76, 795.02) * mm, "end": v(-264.16, 795.02) * mm});
            skLineSegment(sketch, "E78", {"start": v(-264.16, 795.02) * mm, "end": v(-264.16, 909.32) * mm});
            skLineSegment(sketch, "E79", {"start": v(-264.16, 909.32) * mm, "end": v(-162.56, 909.32) * mm});
            skLineSegment(sketch, "E80", {"start": v(-162.56, 909.32) * mm, "end": v(-162.56, 1016) * mm});
            skLineSegment(sketch, "E81", {"start": v(-162.56, 1016) * mm, "end": v(-127, 1016) * mm});
            skLineSegment(sketch, "E82", {"start": v(-469.9, 431.8) * mm, "end": v(-127, 851.73) * mm});
            skLineSegment(sketch, "E83", {"start": v(-317.5, 378.46) * mm, "end": v(-317.5, 243.84) * mm});
            skLineSegment(sketch, "E84", {"start": v(-317.5, 243.84) * mm, "end": v(-203.2, 243.84) * mm});
            skLineSegment(sketch, "E85", {"start": v(-203.2, 243.84) * mm, "end": v(-203.2, 106.68) * mm});
            skLineSegment(sketch, "E86", {"start": v(-127, 5.08) * mm, "end": v(-51.75, 5.08) * mm});
            skLineSegment(sketch, "E87", {"start": v(-127, 5.08) * mm, "end": v(-127, -25.4) * mm});
            skLineSegment(sketch, "E88", {"start": v(-317.5, 378.46) * mm, "end": v(-393.7, 378.46) * mm});
            skLineSegment(sketch, "E89", {"start": v(-393.7, 378.46) * mm, "end": v(-393.7, 431.8) * mm});
            skLineSegment(sketch, "E90", {"start": v(-469.9, 558.8) * mm, "end": v(-393.7, 558.8) * mm});
            skLineSegment(sketch, "E91", {"start": v(-393.7, 558.8) * mm, "end": v(-393.7, 431.8) * mm});
            skLineSegment(sketch, "E92", {"start": v(-203.2, 106.68) * mm, "end": v(-127, 106.68) * mm});
            skLineSegment(sketch, "E93", {"start": v(-127, 106.68) * mm, "end": v(-127, -25.4) * mm});
            skLineSegment(sketch, "E94", {"start": v(-469.9, 678.18) * mm, "end": v(-484.14, 678.18) * mm});
            skLineSegment(sketch, "E95", {"start": v(-484.14, 678.18) * mm, "end": v(-484.14, 431.8) * mm});
            skLineSegment(sketch, "E96", {"start": v(-484.14, 431.8) * mm, "end": v(-469.9, 431.8) * mm});
            skLineSegment(sketch, "E97", {"start": v(-469.9, 431.8) * mm, "end": v(-484.14, 431.8) * mm});
            skLineSegment(sketch, "E98", {"start": v(-484.14, 431.8) * mm, "end": v(-484.14, 558.8) * mm});
            skLineSegment(sketch, "E99", {"start": v(-484.14, 558.8) * mm, "end": v(-469.9, 558.8) * mm});
            skLineSegment(sketch, "E100", {"start": v(-484.14, 431.8) * mm, "end": v(-127, -25.4) * mm});
            skLineSegment(sketch, "E101", {"start": v(-469.9, 558.8) * mm, "end": v(-484.14, 558.8) * mm});
            skLineSegment(sketch, "E102", {"start": v(-484.14, 558.8) * mm, "end": v(-484.14, 431.8) * mm});
            skSolve(sketch);
        }
        {
            var Q0;
            {var subQ5=sQuery(id+"F10.wireOp",EDGE,"E75");Q0=makeQuery(id+"F10.imprint","IMPRINT",FACE,{"disambiguationData":[TD([[makeQuery(id+"F10.imprint","IMPRINT",EDGE,{"derivedFrom":subQ5}),-1.0]])]});}
            var Q1;
            {var subQ0=sQuery(id+"F10.wireOp",EDGE,"E94");Q1=makeQuery(id+"F10.imprint","IMPRINT",FACE,{"disambiguationData":[TD([[makeQuery(id+"F10.imprint","IMPRINT",EDGE,{"derivedFrom":subQ0}),1.0]])]});}
            var Q2;
            {var subQ3=sQuery(id+"F10.wireOp",EDGE,"E90");Q2=makeQuery(id+"F10.imprint","IMPRINT",FACE,{"disambiguationData":[TD([[makeQuery(id+"F10.imprint","IMPRINT",EDGE,{"derivedFrom":subQ3}),-1.0]])]});}
            var Q3;
            Q3=makeQuery(id+"F1.opExtrude","SWEPT_BODY",BODY,{"disambiguationData":[OSD([sQuery(id+"F0.wireOp",EDGE,"E0.top"),sQuery(id+"F0.wireOp",EDGE,"E0.left"),sQuery(id+"F0.wireOp",EDGE,"E6.0"),sQuery(id+"F0.wireOp",EDGE,"E7.0"),sQuery(id+"F0.wireOp",EDGE,"E8.0"),sQuery(id+"F0.wireOp",EDGE,"E14"),sQuery(id+"F0.wireOp",EDGE,"E15"),sQuery(id+"F0.wireOp",EDGE,"E16"),sQuery(id+"F0.wireOp",EDGE,"E21"),sQuery(id+"F0.wireOp",EDGE,"E26.2"),sQuery(id+"F0.wireOp",EDGE,"E27.0"),sQuery(id+"F0.wireOp",EDGE,"E27.1"),sQuery(id+"F0.wireOp",EDGE,"E27.2"),sQuery(id+"F0.wireOp",EDGE,"E29.0"),sQuery(id+"F0.wireOp",EDGE,"E33.0"),sQuery(id+"F0.wireOp",EDGE,"E36"),sQuery(id+"F0.wireOp",EDGE,"E37"),sQuery(id+"F0.wireOp",EDGE,"E40"),sQuery(id+"F0.wireOp",EDGE,"E43"),sQuery(id+"F0.wireOp",EDGE,"E44"),sQuery(id+"F0.wireOp",EDGE,"E45.1"),sQuery(id+"F0.wireOp",EDGE,"E49.0"),sQuery(id+"F0.wireOp",EDGE,"E51.0"),sQuery(id+"F0.wireOp",EDGE,"E52.0"),sQuery(id+"F0.wireOp",EDGE,"E56"),sQuery(id+"F0.wireOp",EDGE,"E58"),sQuery(id+"F0.wireOp",EDGE,"E60.0")])]});
            extrude(context, id + "F11", {"entities" : qUnion([Q0, Q1, Q2]), "endBound" : BoundingType.UP_TO_BODY, "oppositeDirection" : true, "endBoundEntityBody" : qUnion([Q3]), "depth" : 25.4 * mm});
        }
        {
            var Q0;
            Q0=makeQuery(id+"F10.imprint","IMPRINT",FACE,{"disambiguationData":[TD([[makeQuery(id+"F10.imprint","IMPRINT",EDGE,{"derivedFrom":sQuery(id+"F10.wireOp",EDGE,"E83")}),-1.0]])]});
            var Q1;
            {var subQ0=sQuery(id+"F10.wireOp",EDGE,"E85");var subQ1=sQuery(id+"F10.wireOp",EDGE,"E84");var subQ2=makeQuery(id+"F10.imprint","INTERSECT",VERTEX,{"derivedFrom":[subQ1,subQ0]});Q1=makeQuery(id+"F10.imprint","IMPRINT",FACE,{"disambiguationData":[TD([[makeQuery(id+"F10.imprint","IMPRINT",EDGE,{"disambiguationData":[TD([[subQ2,1.0]])],"derivedFrom":subQ1}),-1.0]])]});}
            var Q2;
            {var subQ3=sQuery(id+"F10.wireOp",EDGE,"E90");Q2=makeQuery(id+"F10.imprint","IMPRINT",FACE,{"disambiguationData":[TD([[makeQuery(id+"F10.imprint","IMPRINT",EDGE,{"derivedFrom":subQ3}),-1.0]])]});}
            var Q3;
            Q3=makeQuery(id+"F1.opExtrude","SWEPT_BODY",BODY,{"disambiguationData":[OSD([sQuery(id+"F0.wireOp",EDGE,"E0.top"),sQuery(id+"F0.wireOp",EDGE,"E0.left"),sQuery(id+"F0.wireOp",EDGE,"E6.0"),sQuery(id+"F0.wireOp",EDGE,"E7.0"),sQuery(id+"F0.wireOp",EDGE,"E8.0"),sQuery(id+"F0.wireOp",EDGE,"E14"),sQuery(id+"F0.wireOp",EDGE,"E15"),sQuery(id+"F0.wireOp",EDGE,"E16"),sQuery(id+"F0.wireOp",EDGE,"E21"),sQuery(id+"F0.wireOp",EDGE,"E26.2"),sQuery(id+"F0.wireOp",EDGE,"E27.0"),sQuery(id+"F0.wireOp",EDGE,"E27.1"),sQuery(id+"F0.wireOp",EDGE,"E27.2"),sQuery(id+"F0.wireOp",EDGE,"E29.0"),sQuery(id+"F0.wireOp",EDGE,"E33.0"),sQuery(id+"F0.wireOp",EDGE,"E36"),sQuery(id+"F0.wireOp",EDGE,"E37"),sQuery(id+"F0.wireOp",EDGE,"E40"),sQuery(id+"F0.wireOp",EDGE,"E43"),sQuery(id+"F0.wireOp",EDGE,"E44"),sQuery(id+"F0.wireOp",EDGE,"E45.1"),sQuery(id+"F0.wireOp",EDGE,"E49.0"),sQuery(id+"F0.wireOp",EDGE,"E51.0"),sQuery(id+"F0.wireOp",EDGE,"E52.0"),sQuery(id+"F0.wireOp",EDGE,"E56"),sQuery(id+"F0.wireOp",EDGE,"E58"),sQuery(id+"F0.wireOp",EDGE,"E60.0")])]});
            extrude(context, id + "F12", {"entities" : qUnion([Q0, Q1, Q2]), "endBound" : BoundingType.UP_TO_BODY, "endBoundEntityBody" : qUnion([Q3]), "depth" : 25.4 * mm});
        }
    });
